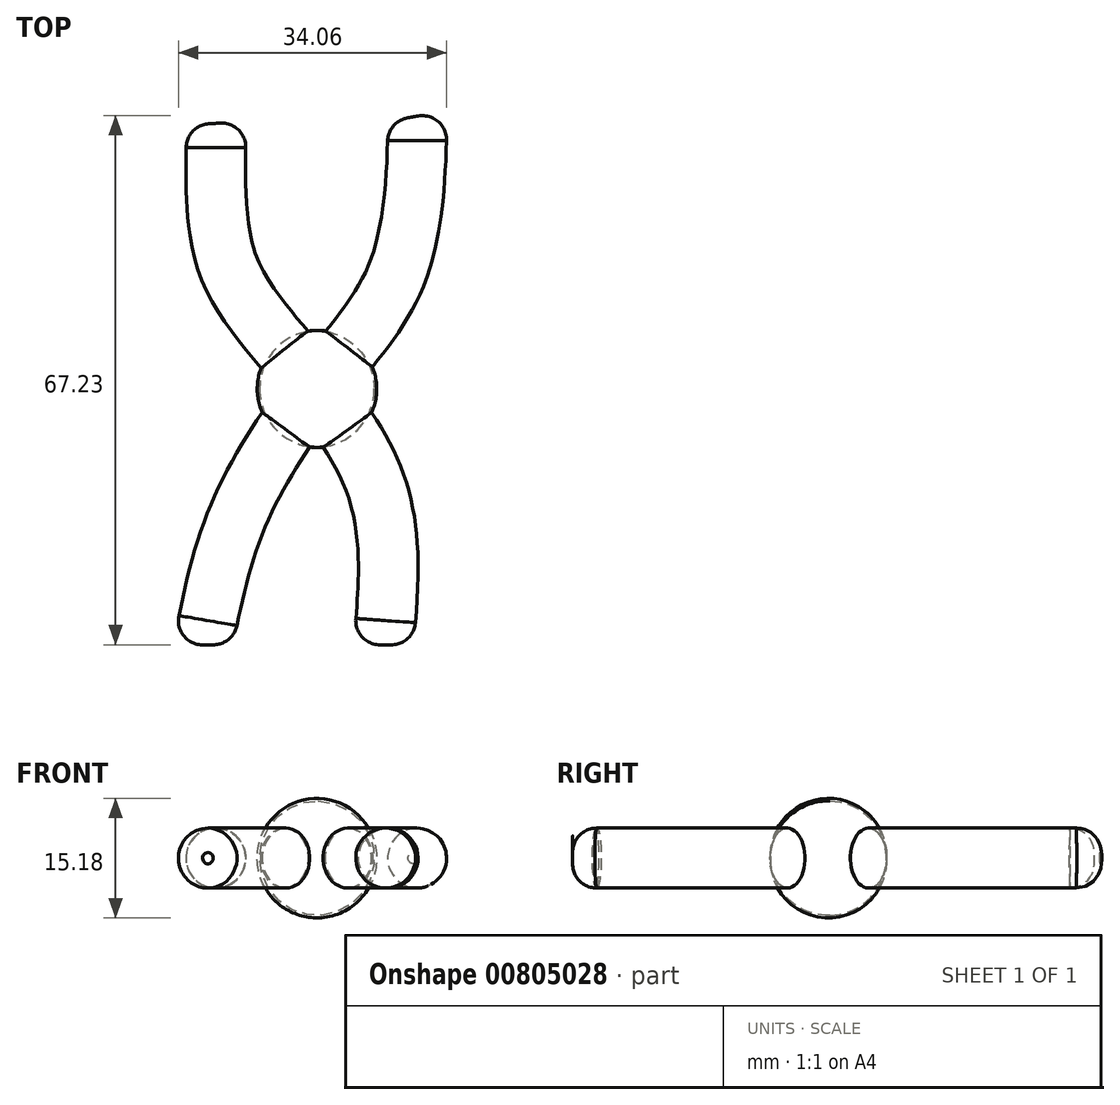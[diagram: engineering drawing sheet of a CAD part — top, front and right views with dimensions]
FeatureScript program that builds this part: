
annotation { "Feature Type Name" : "Feature", "Feature Type Description" : "" }
export const myFeature = defineFeature(function(context is Context, id is Id, definition is map)
    precondition{}
    {
        {
            var Q0;
            Q0=qCreatedBy(makeId("Front.planeOp"),FACE);
            var sketch = newSketch(context, id + "F0", { "sketchPlane" : qUnion([Q0])});
            skCircle(sketch, "E0", {"center": v(-12.37, 0) * mm, "radius": 3.81 * mm});
            skSolve(sketch);
        }
        {
            var Q0;
            Q0=qCreatedBy(makeId("Top.planeOp"),FACE);
            var sketch = newSketch(context, id + "F1", { "sketchPlane" : qUnion([Q0])});
            skFitSpline(sketch, "E1", {"points": [v(-12.26, 0) * mm, v(-7.84, 16.31) * mm, v(2.3, 32.72) * mm, v(12.26, 46.92) * mm, v(15.02, 67.2) * mm], "startDerivative": vector(13.61, 68.54) * mm, "endDerivative": vector(2.3, 82.52) * mm});
            skSolve(sketch);
        }
        {
            var Q0;
            Q0=makeQuery(id+"F0.imprint","IMPRINT",FACE,{"disambiguationData":[TD([[makeQuery(id+"F0.imprint","IMPRINT",EDGE,{"derivedFrom":sQuery(id+"F0.wireOp",EDGE,"E0")}),1.0]])]});
            var Q1;
            Q1=sQuery(id+"F1.wireOp",EDGE,"E1");
            sweep(context, id + "F2", {"profiles" : qUnion([Q0]), "path" : qUnion([Q1])});
        }
        {
            var Q0;
            Q0=qCreatedBy(makeId("Front.planeOp"),FACE);
            var sketch = newSketch(context, id + "F3", { "sketchPlane" : qUnion([Q0])});
            skCircle(sketch, "E2", {"center": v(10.54, 0) * mm, "radius": 3.81 * mm});
            skSolve(sketch);
        }
        {
            var Q0;
            Q0=qCreatedBy(makeId("Top.planeOp"),FACE);
            var sketch = newSketch(context, id + "F4", { "sketchPlane" : qUnion([Q0])});
            skFitSpline(sketch, "E3", {"points": [v(10.78, 0) * mm, v(9.3, 21.66) * mm, v(-4.89, 41.39) * mm, v(-9.86, 51.53) * mm, v(-10.42, 66.28) * mm], "startDerivative": vector(7.56, 79.3) * mm, "endDerivative": vector(1.76, 69.2) * mm});
            skSolve(sketch);
        }
        {
            var Q0;
            Q0=makeQuery(id+"F3.imprint","IMPRINT",FACE,{"disambiguationData":[TD([[makeQuery(id+"F3.imprint","IMPRINT",EDGE,{"derivedFrom":sQuery(id+"F3.wireOp",EDGE,"E2")}),1.0]])]});
            var Q1;
            Q1=sQuery(id+"F4.wireOp",EDGE,"E3");
            sweep(context, id + "F5", {"operationType" : NewBodyOperationType.ADD, "profiles" : qUnion([Q0]), "path" : qUnion([Q1])});
        }
        {
            var Q0;
            Q0=makeQuery(id+"F2.opSweep","CAP_EDGE",EDGE,{"disambiguationData":[OSD([sQuery(id+"F0.wireOp",EDGE,"E0"),sQuery(id+"F1.wireOp",VERTEX,"E1.start")])],"isStart":true});
            var Q1;
            Q1=makeQuery(id+"F5.opSweep","CAP_EDGE",EDGE,{"disambiguationData":[OSD([sQuery(id+"F3.wireOp",EDGE,"E2"),sQuery(id+"F4.wireOp",VERTEX,"E3.start")])],"isStart":true});
            var Q2;
            Q2=makeQuery(id+"F2.opSweep","CAP_EDGE",EDGE,{"disambiguationData":[OSD([sQuery(id+"F0.wireOp",EDGE,"E0"),sQuery(id+"F1.wireOp",VERTEX,"E1.end")])],"isStart":false});
            var Q3;
            Q3=makeQuery(id+"F5.opSweep","CAP_EDGE",EDGE,{"disambiguationData":[OSD([sQuery(id+"F3.wireOp",EDGE,"E2"),sQuery(id+"F4.wireOp",VERTEX,"E3.end")])],"isStart":false});
            fillet(context, id + "F6", {"entities" : qUnion([Q0, Q1, Q2, Q3]), "radius" : 3.09 * mm, "tangentPropagation" : true, "allowEdgeOverflow" : false});
        }
        {
            var Q0;
            Q0=qCreatedBy(makeId("Top.planeOp"),FACE);
            var sketch = newSketch(context, id + "F7", { "sketchPlane" : qUnion([Q0])});
            skLineSegment(sketch, "E4", {"start": v(2.1, 39.94) * mm, "end": v(2.1, 25.09) * mm});
            skArc(sketch, "E5", {"start": v(2.1, 39.94) * mm, "mid": v(-5.5, 32.51) * mm, "end": v(2.1, 25.09) * mm});
            skSolve(sketch);
        }
        {
            var Q0;
            Q0=makeQuery(id+"F7.imprint","IMPRINT",FACE,{"disambiguationData":[TD([[makeQuery(id+"F7.imprint","IMPRINT",EDGE,{"derivedFrom":sQuery(id+"F7.wireOp",EDGE,"E4")}),-1.0]])]});
            var Q1;
            Q1=sQuery(id+"F7.wireOp",EDGE,"E4");
            revolve(context, id + "F8", {"operationType" : NewBodyOperationType.ADD, "surfaceOperationType" : NewSurfaceOperationType.NEW, "entities" : qUnion([Q0]), "axis" : qUnion([Q1]), "revolveType" : RevolveType.FULL});
        }
    });
